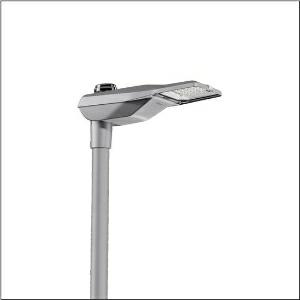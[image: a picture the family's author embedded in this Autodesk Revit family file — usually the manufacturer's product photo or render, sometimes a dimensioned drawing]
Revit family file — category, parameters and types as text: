
# Revit family: streetlight_sl_21_micro___st1_5a_5xe5p47n08db_8f26
name_source: partatom
category: Lighting Fixtures
units: mm (PartAtom-declared; Revit-internal decimal feet)

## family parameters
Cut with Voids When Loaded = No
Host = Face
Light Source = No
Part Type = Normal
Room Calculation Point = No
Round Connector Dimension = Use Diameter
Shared = No

## types (1)
- --- (1 x LED, 5230 lm, 39.1 W, 4000K)
    Apparent Load = 39 VA
    CIE Flux Codes = 22 53 95 100 100
    Color Rendering = 70
    Color Temperature = 4000K
    Default Elevation = 1800 mm
    Description = Streetlight SL 21 micro, mast luminaire, primary light control with lens, of PMMA, primary optical cover: cover, of toughened safety glass, transparent, light distribution: ST1.5a, light emission: direct distribution, primary light characteristic: asymmetric, installation type: post-top, LED, 3G 1.5mm², High Power LED, rated luminous flux: 5.230lm, luminous efficacy: 134lm/W, light colour: 740, colour temperature: 4000K, control gear: NEMA (7pin), control: overheat protection, pre-setting: linear dimming characteristic, constant luminous flux control, time-dependent luminous flux control, flexible luminous flux parameterisation, mains connection: 230..240V, AC, 50/60Hz, connection cable pre-assembled, cable length: 6,5m, wiring characteristics: H07RN-F, start of lifetime: 39W, end of service life: 41W, reduction: 18W, luminaire housing, of diecast aluminium (EN AC-44300), powder-coated, Siteco® metallic grey (DB 702S), corrosivity category C5 mid according to DIN EN ISO 12944, multi-level sealing system, sealing non-destructively replaceable, inclination adjustable: 0°, 5°, 10°, 15°, length: 528mm, width: 235mm, height: 110mm, spigot size: 76/60mm (post-top), mounting height: 4..8m, protection rating (complete): IP66, insulation class (complete): insulation class I (protective earthing), certification: CE, ENEC, ENEC+, VDE, impact resistance: IK10, permissible operating ambient temperature for outdoor applications: -40..+50°C, standard-compliant lighting for roads and squares, packaging unit: 1 piece

Light Distribution: ST1.5a
    Height = 110 mm
    Lamp = 1 x LED
    Lamp Light Flux = 5230 lm
    Lamp Power = 39.1 W
    Lamp count = 1
    Length = 528 mm
    Luminous efficacy = 134 lm/W
    Manufacturer = Siteco
    ModVariant = No
    Model = 5XE5P47N08DB
    Number of Poles = 1
    OnlyDefault = Yes
    Power Factor = 1
    Product Name = Streetlight SL 21 micro | ST1.5a
    Product group = mast luminaire | pylon top
    ProductGroupID = 6100
    Protection Class = Protection class I
    Protection Degree = IP 66
    RLX_Detail_Level = 1
    RLX_Emergency_Light_Flux = 0 lm
    RLX_Emergency_Type = 0
    RLX_Emergency_Type_DB = No
    RlxData = <blob elided: 103545 chars, md5=e0fd20e9>
    Socket = socket
    Standby Power = 0 W
    System Light Flux = 5230 lm
    System Power = 39 W
    Type Comments = factory setting: luminous flux: 100 % | dim-lin: 254 | 765 mA
    Type Image = l_1294375.jpg
    URL = http://relux.com
    VarID = @adj_155175
    Voltage = 0 V
    Weight = 0.00 kg
    Width = 235 mm

## geometry (parser evidence)
native form markers: Blend x4, Sweep x8
no freeform markers — native parametric forms only
